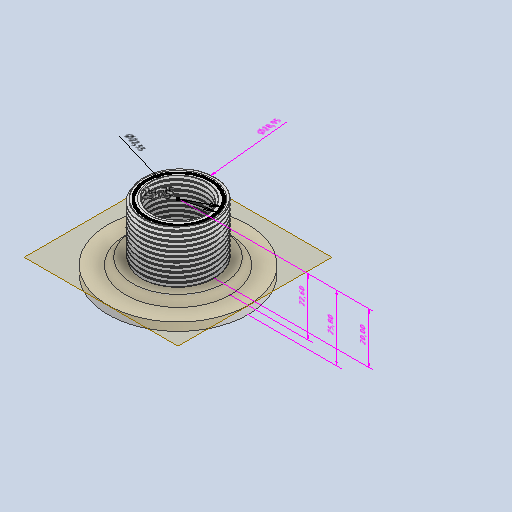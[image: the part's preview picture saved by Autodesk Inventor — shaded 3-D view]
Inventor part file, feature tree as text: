
AUTODESK INVENTOR PART (.ipt)
format: ipt  version: 2023.1 (Build 271208000, 208)  size: 2,065,408 bytes
history: native  units: mm
features: sketch x11, other x6, extrude x3, revolve x3, thread x2, helix x2, plane x1, split x1, rib x1
ambient origin geometry x8: Origin, YZ Plane, XZ Plane, XY Plane, X Axis, Y Axis, Z Axis, Center Point
bodies: Solid1 (feature_tree), Solid2 (feature_tree), Solid3 (feature_tree)
feature tree (30):
  other  "Annotations"
  extrude  "Extrusion1"  Depth=55.0mm
  extrude  "Extrusion2"  Depth=22.55mm
  thread  "Thread1"  [1 undecoded]
  extrude  "Extrusion3"  Depth=25.8mm TaperAngle=0.0deg
  sketch  "Sketch4"  dims[d11=24.15mm d12=22.6mm d13=0.0mm d20=24.75mm]
  plane  "Work Plane2"
  sketch  "Sketch5"  dims[d21=25.75mm d24=2.6mm]
  sketch  "Sketch6"  dims[d27=24.75mm d28=25.75mm d47=20.0mm d48=0.0mm]
  split  "Split3"
  thread  "Thread2"  [1 undecoded]
  rib  "Rib1"
  revolve  "Revolution1"  [1 undecoded]
  helix  "Coil1"  [1 undecoded]
  revolve  "Revolution2"  [1 undecoded]
  revolve  "Revolution3"  [1 undecoded]
  helix  "Coil2"  [1 undecoded]
  sketch  "Sketch1"  dims[d0=22.55mm d1=55.0mm]
  sketch  "Sketch2"  dims[d2=3.2mm d3=0.0mm d4=22.55mm d5=24.15mm]
  sketch  "Sketch3"  dims[d6=22.6mm d7=0.0mm d8=25.8mm d9=0.0mm d10=28.95mm]
  sketch  "Sketch8"  dims[d49=10.0mm d50=1.0mm d51=45.0deg d52=0.0mm d53=1.0mm d54=1.0mm]
  sketch  "Sketch9"  dims[d58=0.378886mm d59=0.21875mm d60=0.109375mm d61=0.189443mm d62=1.75mm]
  sketch  "Sketch10"  dims[d64=60.0deg]
  sketch  "Sketch11"  dims[d67=0.21875mm]
  sketch  "Sketch12"  dims[d69=60.0deg d70=0.0mm d71=1.75175mm d72=29.3mm d73=10.0mm d74=0.0mm d75=0.0mm d76=0.0mm d77=0.0mm d78=0.0mm d79=0.378886mm d80=0.21875mm d81=0.109375mm d82=0.189443mm d83=1.75mm d85=60.0deg d88=0.21875mm d90=60.0deg d91=0.0mm d92=0.0mm d93=1.75175mm d94=23.5mm d95=10.0mm d96=0.0mm d97=0.0mm d98=0.0mm d99=0.0mm d100=0.0mm d14=22.6mm d18=59.957742mm d19=22.55mm d39=25.8mm d55=48.118816mm d56=28.95mm d57=20.0mm d40=0.872665mm d41=0.5mm d42=0.872665mm]
  other  "Linear Dimension 1"
  other  "Diameter Dimension 2"
  other  "Linear Dimension 2"
  other  "Diameter Dimension 3"
  other  "Linear Dimension 3"
note: 7 required parameter values undecoded (feature->parameter linkage not recoverable at this tier; creation-order binding heuristic only, values carry confidence <= 0.55)